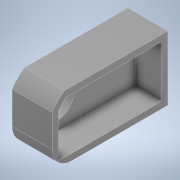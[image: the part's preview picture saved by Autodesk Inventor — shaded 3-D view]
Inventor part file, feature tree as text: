
AUTODESK INVENTOR PART (.ipt)
format: ipt  version: 2022 (Build 260153000, 153)  size: 389,632 bytes
history: mixed  units: in
note: dims shown in document units (in); Inventor stores cm internally (conversion verified against a paired STEP export)
features: extrude x5, sketch x5, other x2, plane x1, fillet x1, imported_body x1
ambient origin geometry x8: Origin, YZ Plane, XZ Plane, XY Plane, X Axis, Y Axis, Z Axis, Center Point
bodies: Solid1 (imported_parasolid)
feature tree (15):
  other  "Repaired Geometry1"
  plane  "Work Plane1"
  extrude  "Extrusion1"  Depth=0.0405in TaperAngle=0.0deg
  extrude  "Extrusion3"  Depth=0.9843in TaperAngle=0.0deg
  extrude  "Extrusion4"  Depth=0.3937in
  extrude  "Extrusion5"  Depth=0.7283in
  extrude  "Extrusion6"  [1 undecoded]
  fillet  "Fillet1"  [1 undecoded]
  sketch  "Sketch2"  dims[d2=1.0236in d3=0.0787in d4=0.0in d5=0.0in d9=0.0405in d10=0.0in]
  other  "96_Teeth_Gear.STEP"
  sketch  "Sketch4"  dims[d11=0.2362in d12=0.9843in d13=0.0in]
  sketch  "Sketch5"  dims[d14=0.3937in d15=0.0in d16=1.2638in]
  sketch  "Sketch6"  dims[d17=0.5118in d18=0.0in d19=0.7283in]
  sketch  "Sketch7"
  imported_body  NMx_Import_Brep_tag  [imported B-rep: ~15 faces, bbox_mm=[38.0, 61.028, 110.0]]
note: 2 required parameter values undecoded (feature->parameter linkage not recoverable at this tier; creation-order binding heuristic only, values carry confidence <= 0.55)
